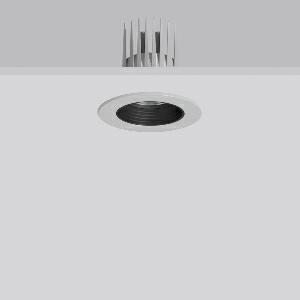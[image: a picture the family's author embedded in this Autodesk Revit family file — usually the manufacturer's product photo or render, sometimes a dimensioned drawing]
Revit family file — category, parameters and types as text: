
# Revit family: heledon_mini_e_901752_004_1_1bdc
name_source: partatom
category: Lighting Fixtures
units: mm (PartAtom-declared; Revit-internal decimal feet)

## family parameters
Cut with Voids When Loaded = No
Host = Face
Light Source = No
Part Type = Normal
Room Calculation Point = No
Round Connector Dimension = Use Diameter
Shared = No

## types (1)
- HELEDON mini E (1 x LED Modul 940, 3200 lm, 4000)
    Apparent Load = 29 VA
    Approval mark = CE
    CIE Flux Codes = 96 100 100 100 100
    Color Rendering = 92
    Color Temperature = 4000
    Default Elevation = 1800 mm
    Description = Series: HELEDON mini
Round recessed downlight. Housing: die-cast aluminium, powder-coated. Black plastic ring and recessed LED to prevent glare from the side. Optical assembly with lens made of plastic (polycarbonate) for the best homogeneous light distribution - can be changed without tools. Best colour rendering index Ra>90. Suitable for Recessed ceiling mounting. Installation without tools thanks to spring fastening system. Including separate LED converter with connecting cable 600 mm.High quality converter without flickering and stroboscopic effect. Through-wiring box (5 pole) available as accessory. The following accessories can be mounted without use of tools: interchangeable lenses, decorative glasses, honeycomb louvre, clear and frosted diffusers, white interchangeable plastic ring. 
Colour: silver
Diameter: 124 mm
Height: 3 mm
Cut-out diameter: 114 mm
Recess height: 170 mm
Luminaire: recess height: 120 mm
Lamp: LED
Socket: without socket
Colour temperature: 4000K
Colour rendering index (CRI): 92
System power: 29 W
Rated luminous flux: 3200 lm
Luminous efficiency: 110 lm/W
Control gear: Regulated power supply
Protection class: II
Type of protection: IP 20
    Height = 0 mm  [stored 0 ft]
    Lamp = 1 x LED Modul 940
    Lamp Light Flux = 3200 lm
    Lamp count = 1
    Length = 124 mm  [stored 0.406824 ft]
    Lifetime = 50000 h
    Luminous efficacy = 110 lm/W
    Manufacturer = RZB
    ModVariant = No
    Model = 901752.004.1
    Mounting Place = Ceiling
    Mounting Type = Recessed
    Number of Poles = 1
    OnlyDefault = Yes
    Power Factor = 1
    Product Name = HELEDON mini E
    Product group = Recessed downlights
    ProductGroupID = 402
    Protection Class = Protection class II
    Protection Degree = IP 20
    RLX_Detail_Level = 1
    RLX_Emergency_Light_Flux = 0 lm
    RLX_Emergency_Type = 0
    RLX_Emergency_Type_DB = No
    RlxData = <blob elided: 127193 chars, md5=2c54bd48>
    Socket = socket
    Standby Power = 0 W
    System Light Flux = 3200 lm
    System Power = 29 W
    Type Comments = Product without accessories
    Type Image = 901656.004.jpg
    URL = http://relux.com
    VarID = ---
    Voltage = 230 V
    Voltage Range = 220-240 V
    Weight = 0.00 kg
    Width = 0 mm  [stored 0 ft]

note: [stored X ft] marks values corroborated as IEEE doubles in the binary element streams (Revit-internal decimal feet)

## geometry (parser evidence)
native form markers: Blend x4, Sweep x11
no freeform markers — native parametric forms only
